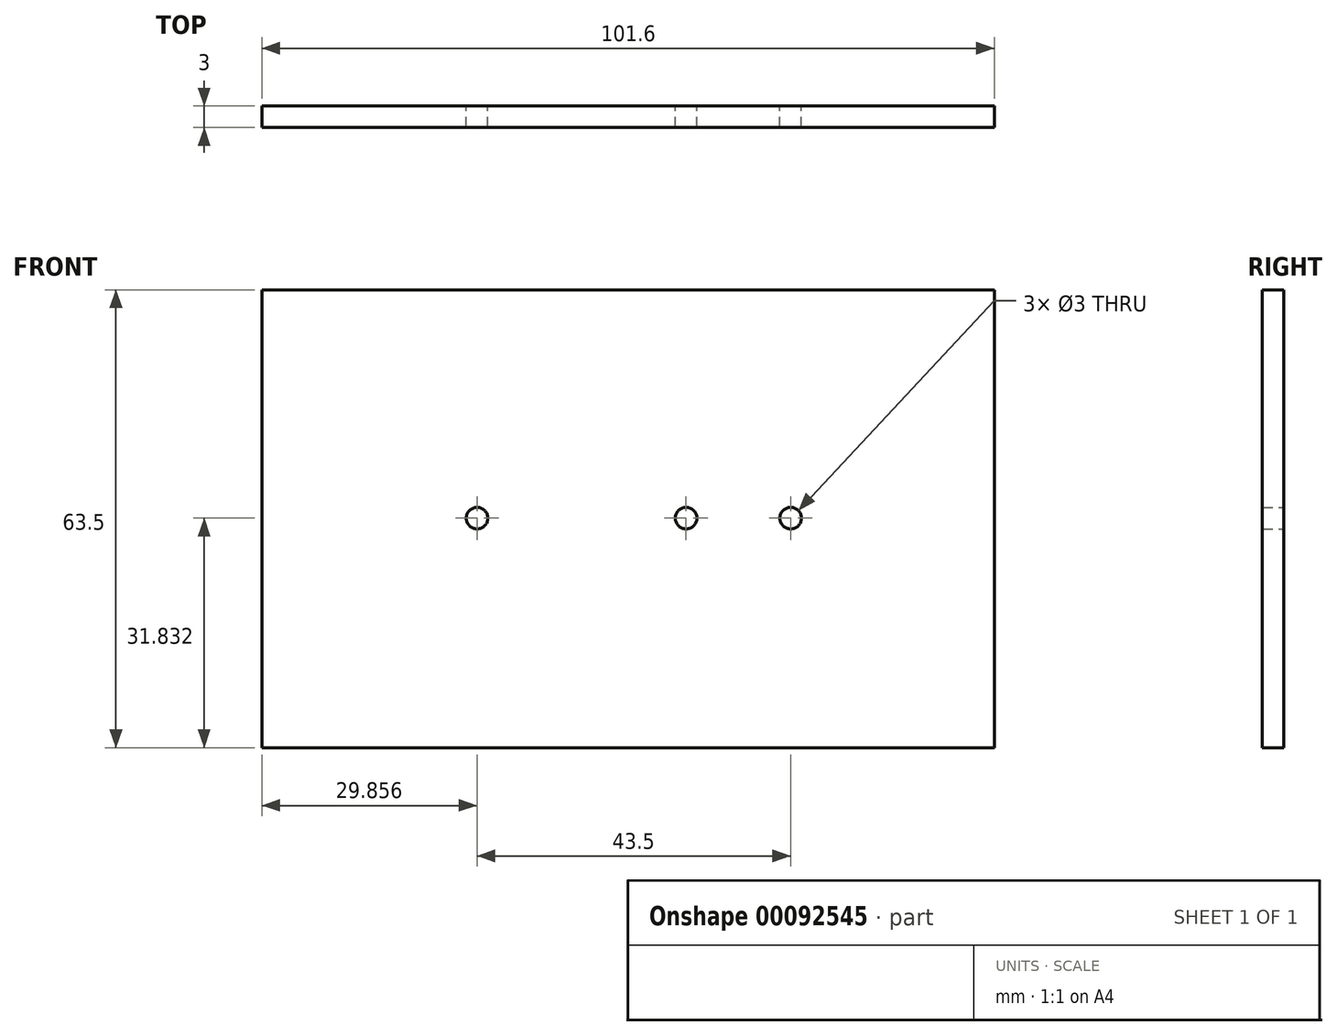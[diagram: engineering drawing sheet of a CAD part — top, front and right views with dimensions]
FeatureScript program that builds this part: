
annotation { "Feature Type Name" : "Feature", "Feature Type Description" : "" }
export const myFeature = defineFeature(function(context is Context, id is Id, definition is map)
    precondition{}
    {
        {
            var Q0;
            Q0=qCreatedBy(makeId("Front.planeOp"),FACE);
            var sketch = newSketch(context, id + "F0", { "sketchPlane" : qUnion([Q0])});
            skLineSegment(sketch, "E0.bottom", {"start": v(-52.7, 27.04) * mm, "end": v(48.9, 27.04) * mm});
            skLineSegment(sketch, "E0.top", {"start": v(-52.7, -36.46) * mm, "end": v(48.9, -36.46) * mm});
            skLineSegment(sketch, "E0.left", {"start": v(-52.7, 27.04) * mm, "end": v(-52.7, -36.46) * mm});
            skLineSegment(sketch, "E0.right", {"start": v(48.9, 27.04) * mm, "end": v(48.9, -36.46) * mm});
            skPoint(sketch, "E1", {"position": v(-22.85, -4.63) * mm});
            skPoint(sketch, "E2", {"position": v(6.15, -4.63) * mm});
            skPoint(sketch, "E3", {"position": v(20.65, -4.63) * mm});
            skCircle(sketch, "E4", {"center": v(-22.85, -4.63) * mm, "radius": 1.5 * mm});
            skCircle(sketch, "E5", {"center": v(6.15, -4.63) * mm, "radius": 1.5 * mm});
            skCircle(sketch, "E6", {"center": v(20.65, -4.63) * mm, "radius": 1.5 * mm});
            skSolve(sketch);
        }
        {
            var Q0;
            Q0 = qSketchRegion(id + "F0", true);
            var Q1;
            Q1=makeQuery(id+"F0.imprint","IMPRINT",FACE,{"disambiguationData":[TD([[makeQuery(id+"F0.imprint","IMPRINT",EDGE,{"derivedFrom":sQuery(id+"F0.wireOp",EDGE,"E0.bottom")}),-1.0]])]});
            extrude(context, id + "F1", {"entities" : qUnion([Q0, Q1]), "depth" : 3 * mm});
        }
    });
